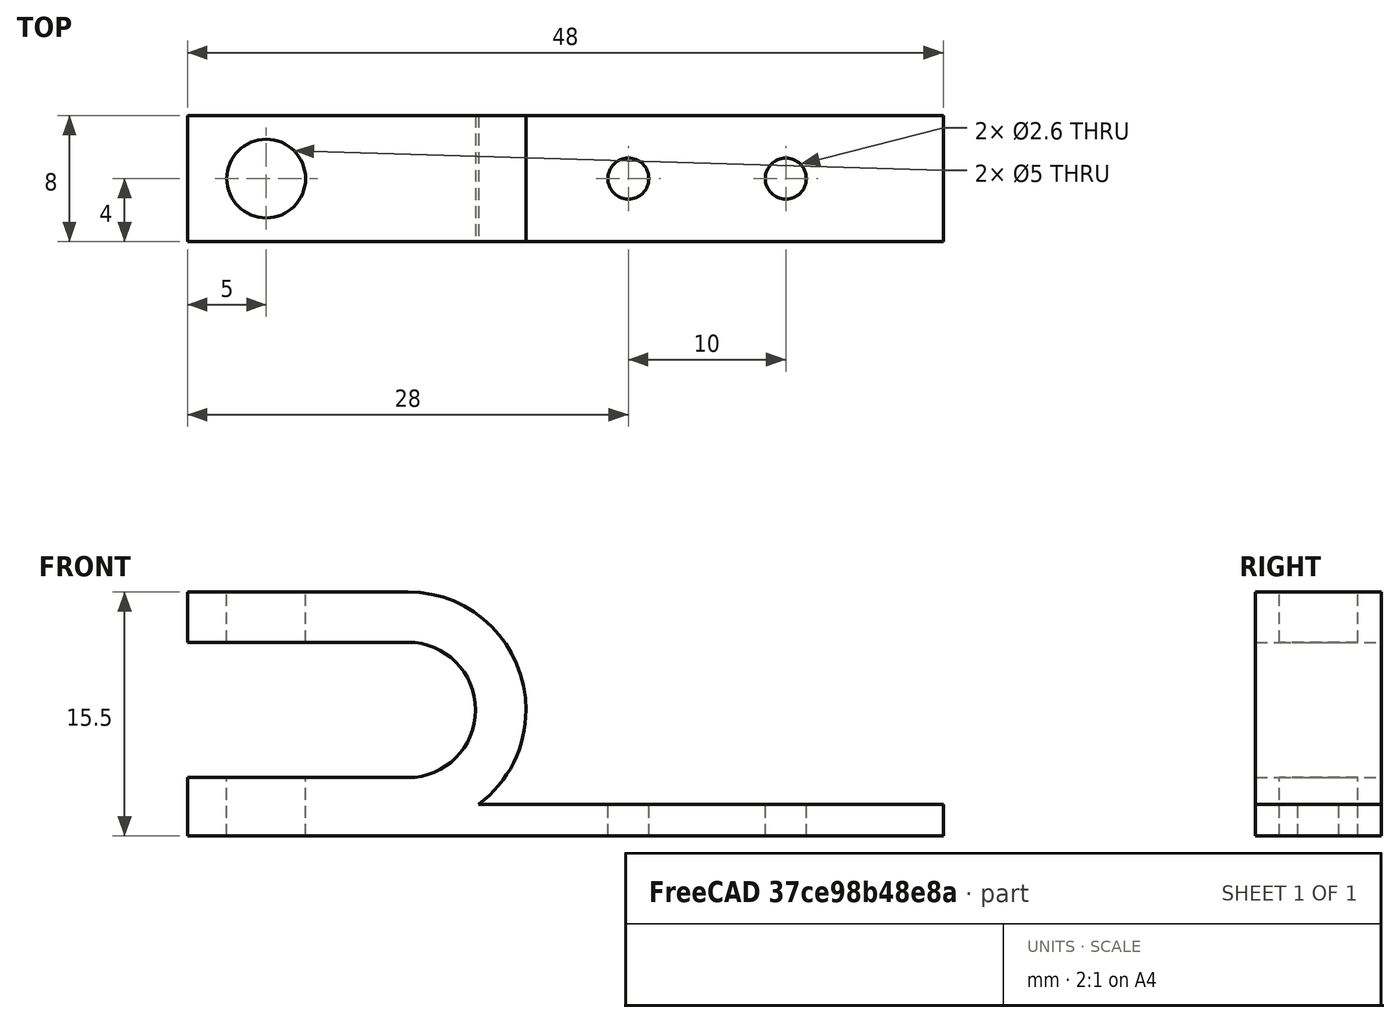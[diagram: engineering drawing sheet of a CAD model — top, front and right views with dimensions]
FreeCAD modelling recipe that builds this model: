
FCSTD DOCUMENT  (FreeCAD 0.16R6706 (Git))
Label: Soporte final de carrera 2
License: All rights reserved
LicenseURL: http://en.wikipedia.org/wiki/All_rights_reserved
objects: Part::Cut×6, Part::Cylinder×5, Part::Box×4, Part::Fuse×1, Part::MultiFuse×1, Part::Feature×1
note: 18 computed .brp shape members not serialized (recipe doc carries the construction recipe); baked Part::Feature solids carry a one-line shape summary decoded from their .brp

FEATURE [Part::Cylinder] Cylinder005  label="Cilindro005"
  Angle = 360
  Height = 8
  Placement = pos=(5,8,8) rot=(1,0,0;1.5708rad)
  Radius = 7.5
FEATURE [Part::Cylinder] Cylinder006  label="Cilindro006"
  Angle = 360
  Height = 8
  Placement = pos=(5,8,8) rot=(1,0,0;1.5708rad)
  Radius = 4.3
FEATURE [Part::Cut] Cut004
  Base = -> Cylinder005
  Tool = -> Cylinder006
FEATURE [Part::Box] Box  label="Cubo"
  Height = 2
  Length = 48
  Placement = pos=(-9,0,0) rot=(0,0,1;0rad)
  Width = 8
FEATURE [Part::Box] Box004  label="Cubo004"
  Height = 15.5
  Length = 14
  Placement = pos=(-9,0,0) rot=(0,0,1;0rad)
  Width = 8
FEATURE [Part::Box] Box005  label="Cubo005"
  Height = 8.6
  Length = 14
  Placement = pos=(-9,0,3.7) rot=(0,0,1;0rad)
  Width = 8
FEATURE [Part::Cut] Cut003
  Base = -> Box004
  Tool = -> Box005
FEATURE [Part::Fuse] Fusion001003
  Base = -> Box
  Tool = -> Cut003
FEATURE [Part::Box] Box006  label="Cubo006"
  Height = 8.6
  Length = 14
  Placement = pos=(-9,0,3.7) rot=(0,0,1;0rad)
  Width = 8
FEATURE [Part::Cut] Cut
  Base = -> Cut004
  Tool = -> Box006
FEATURE [Part::MultiFuse] Fusion
  Shapes = -> [Fusion001003,Cut]
FEATURE [Part::Feature] Fusion001004
  shape: bbox 48 x 8 x 15.5 mm, 12 faces (baked)
FEATURE [Part::Cylinder] Cylinder003  label="Cilindro003"
  Angle = 360
  Height = 17
  Placement = pos=(19,4,-1) rot=(0,0,1;0rad)
  Radius = 1.3
FEATURE [Part::Cylinder] Cylinder004  label="Cilindro004"
  Angle = 360
  Height = 17
  Placement = pos=(29,4,-1) rot=(0,0,1;0rad)
  Radius = 1.3
FEATURE [Part::Cut] Cut005
  Base = -> Fusion001004
  Tool = -> Cylinder003
FEATURE [Part::Cut] Cut006
  Base = -> Cut005
  Tool = -> Cylinder004
FEATURE [Part::Cylinder] Cylinder002  label="Cilindro002"
  Angle = 360
  Height = 17
  Placement = pos=(-4,4,-1) rot=(0,0,1;0rad)
  Radius = 2.5
FEATURE [Part::Cut] Cut007
  Base = -> Cut006
  Tool = -> Cylinder002
